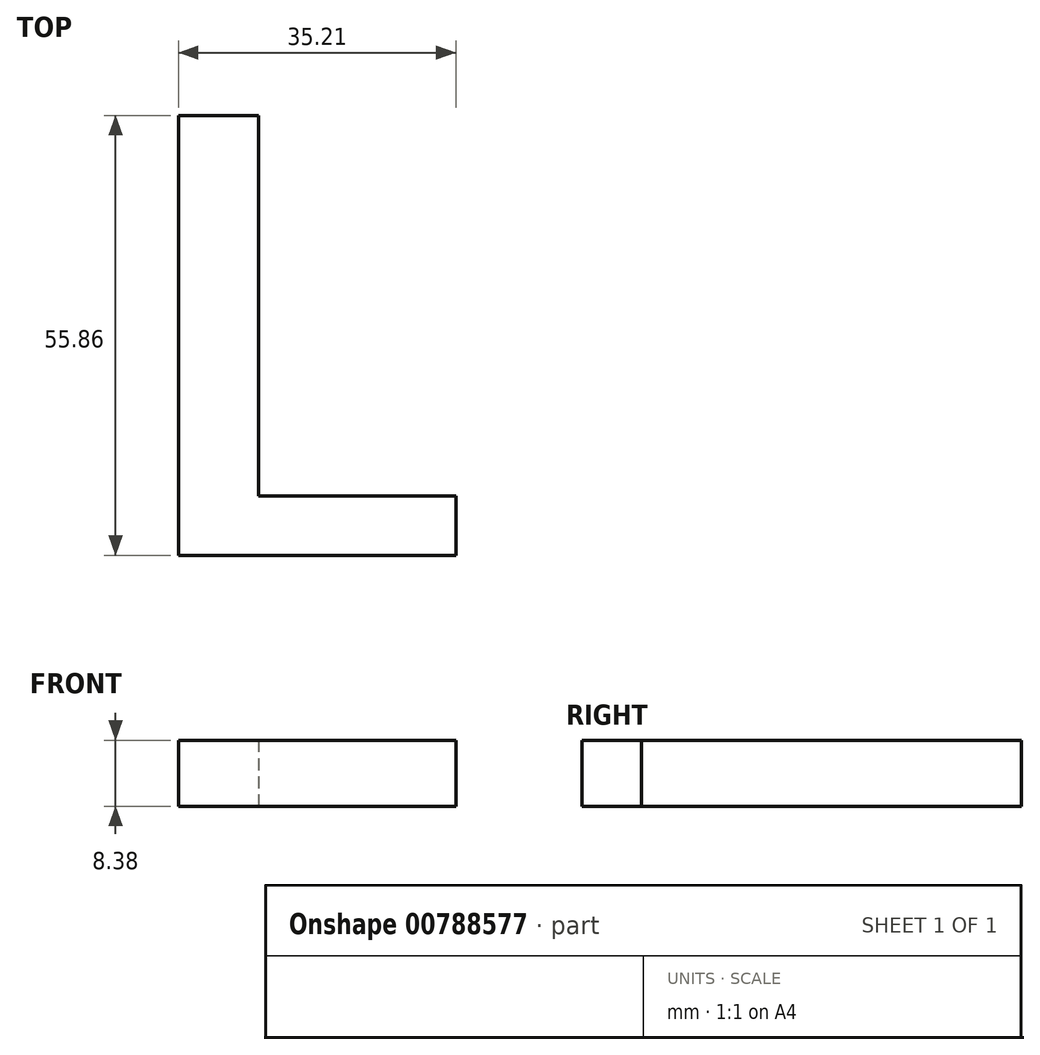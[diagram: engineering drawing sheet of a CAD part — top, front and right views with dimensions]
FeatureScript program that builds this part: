
annotation { "Feature Type Name" : "Feature", "Feature Type Description" : "" }
export const myFeature = defineFeature(function(context is Context, id is Id, definition is map)
    precondition{}
    {
        {
            var Q0;
            Q0=qCreatedBy(makeId("Top.planeOp"),FACE);
            var sketch = newSketch(context, id + "F0", { "sketchPlane" : qUnion([Q0])});
            skLineSegment(sketch, "E0", {"start": v(-48.02, 35.67) * mm, "end": v(-48.02, -20.19) * mm});
            skLineSegment(sketch, "E1", {"start": v(-48.02, -20.19) * mm, "end": v(-12.81, -20.19) * mm});
            skLineSegment(sketch, "E2", {"start": v(-12.81, -20.19) * mm, "end": v(-12.81, -12.63) * mm});
            skLineSegment(sketch, "E3", {"start": v(-48.02, 35.67) * mm, "end": v(-37.88, 35.67) * mm});
            skLineSegment(sketch, "E4", {"start": v(-37.88, 35.67) * mm, "end": v(-37.88, -12.63) * mm});
            skLineSegment(sketch, "E5", {"start": v(-37.88, -12.63) * mm, "end": v(-12.81, -12.63) * mm});
            skSolve(sketch);
        }
        {
            var Q0;
            Q0=makeQuery(id+"F0.imprint","IMPRINT",FACE,{"disambiguationData":[TD([[makeQuery(id+"F0.imprint","IMPRINT",EDGE,{"derivedFrom":sQuery(id+"F0.wireOp",EDGE,"E0")}),1.0]])]});
            extrude(context, id + "F1", {"entities" : qUnion([Q0]), "depth" : 8.38 * mm, "offsetDistance" : 25.4 * mm});
        }
    });
